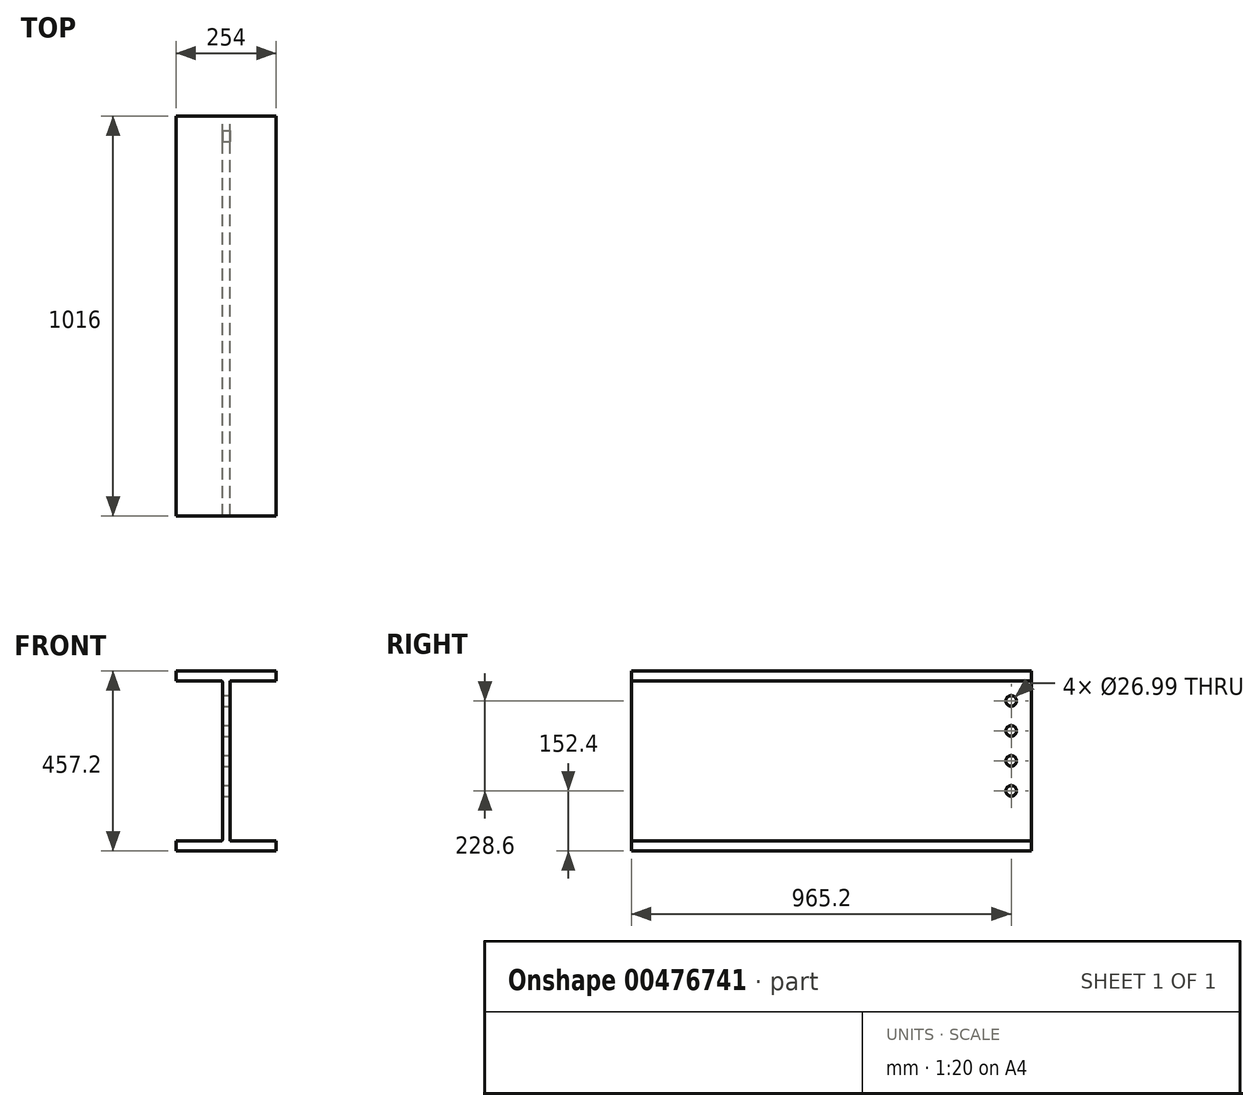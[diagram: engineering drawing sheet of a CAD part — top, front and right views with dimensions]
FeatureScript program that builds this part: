
annotation { "Feature Type Name" : "Feature", "Feature Type Description" : "" }
export const myFeature = defineFeature(function(context is Context, id is Id, definition is map)
    precondition{}
    {
        {
            var Q0;
            Q0=qCreatedBy(makeId("Front.planeOp"),FACE);
            var sketch = newSketch(context, id + "F0", { "sketchPlane" : qUnion([Q0])});
            skLineSegment(sketch, "E0", {"start": v(127, -203.2) * mm, "end": v(12.06, -203.2) * mm});
            skLineSegment(sketch, "E1", {"start": v(9.52, -200.66) * mm, "end": v(9.52, 200.66) * mm});
            skLineSegment(sketch, "E2", {"start": v(12.06, 203.2) * mm, "end": v(127, 203.2) * mm});
            skLineSegment(sketch, "E3", {"start": v(-127, 203.2) * mm, "end": v(-12.06, 203.2) * mm});
            skLineSegment(sketch, "E4", {"start": v(-9.53, 200.66) * mm, "end": v(-9.53, -200.66) * mm});
            skLineSegment(sketch, "E5", {"start": v(-12.06, -203.2) * mm, "end": v(-127, -203.2) * mm});
            skLineSegment(sketch, "E6", {"start": v(0, 0) * mm, "end": v(-9.52, 0) * mm, "construction": true});
            skLineSegment(sketch, "E7", {"start": v(0, 0) * mm, "end": v(9.52, 0) * mm, "construction": true});
            skLineSegment(sketch, "E8", {"start": v(0, 0) * mm, "end": v(0, 228.6) * mm, "construction": true});
            skLineSegment(sketch, "E9", {"start": v(0, 0) * mm, "end": v(0, -228.6) * mm, "construction": true});
            skPoint(sketch, "E10.visualSharp", {"position": v(-9.53, 203.2) * mm});
            skArc(sketch, "E10.filletArc", {"start": v(-9.52, 200.66) * mm, "mid": v(-10.27, 202.46) * mm, "end": v(-12.06, 203.2) * mm});
            skPoint(sketch, "E11.visualSharp", {"position": v(9.53, 203.2) * mm});
            skArc(sketch, "E11.filletArc", {"start": v(12.06, 203.2) * mm, "mid": v(10.27, 202.46) * mm, "end": v(9.52, 200.66) * mm});
            skPoint(sketch, "E12.visualSharp", {"position": v(9.53, -203.2) * mm});
            skArc(sketch, "E12.filletArc", {"start": v(9.52, -200.66) * mm, "mid": v(10.27, -202.46) * mm, "end": v(12.06, -203.2) * mm});
            skPoint(sketch, "E13.visualSharp", {"position": v(-9.53, -203.2) * mm});
            skArc(sketch, "E13.filletArc", {"start": v(-12.06, -203.2) * mm, "mid": v(-10.27, -202.46) * mm, "end": v(-9.52, -200.66) * mm});
            skPoint(sketch, "E14.visualSharp", {"position": v(-127, 228.6) * mm});
            skPoint(sketch, "E15.visualSharp", {"position": v(127, 228.6) * mm});
            skPoint(sketch, "E16.visualSharp", {"position": v(127, 203.2) * mm});
            skPoint(sketch, "E17.visualSharp", {"position": v(127, -228.6) * mm});
            skPoint(sketch, "E18.visualSharp", {"position": v(-127, -203.2) * mm});
            skPoint(sketch, "E19.visualSharp", {"position": v(-127, -228.6) * mm});
            skLineSegment(sketch, "E20", {"start": v(127, -203.2) * mm, "end": v(127, -228.6) * mm});
            skLineSegment(sketch, "E21", {"start": v(-127, -203.2) * mm, "end": v(-127, -228.6) * mm});
            skLineSegment(sketch, "E22", {"start": v(-127, 228.6) * mm, "end": v(-127, 203.2) * mm});
            skLineSegment(sketch, "E23", {"start": v(127, 228.6) * mm, "end": v(127, 203.2) * mm});
            skLineSegment(sketch, "E24", {"start": v(-127, 228.6) * mm, "end": v(127, 228.6) * mm});
            skLineSegment(sketch, "E25", {"start": v(-127, -228.6) * mm, "end": v(127, -228.6) * mm});
            skSolve(sketch);
        }
        {
            var Q0;
            Q0=makeQuery(id+"F0.imprint","IMPRINT",FACE,{"disambiguationData":[TD([[makeQuery(id+"F0.imprint","IMPRINT",EDGE,{"derivedFrom":sQuery(id+"F0.wireOp",EDGE,"E0")}),1.0]])]});
            extrude(context, id + "F1", {"entities" : qUnion([Q0]), "endBound" : BoundingType.SYMMETRIC, "depth" : 1016 * mm});
        }
        {
            var Q0;
            Q0=makeQuery(id+"F1.opExtrude","SWEPT_FACE",FACE,{"disambiguationData":[OSD([sQuery(id+"F0.wireOp",EDGE,"E1")])]});
            var sketch = newSketch(context, id + "F2", { "sketchPlane" : qUnion([Q0])});
            skPoint(sketch, "E26", {"position": v(457.2, 152.4) * mm});
            skPoint(sketch, "E27", {"position": v(457.2, 76.2) * mm});
            skPoint(sketch, "E28", {"position": v(457.2, 0) * mm});
            skPoint(sketch, "E29", {"position": v(457.2, -76.2) * mm});
            skSolve(sketch);
        }
        {
            var Q0;
            Q0=sQuery(id+"F2.wireOp",VERTEX,"E26");
            var Q1;
            Q1=sQuery(id+"F2.wireOp",VERTEX,"E27");
            var Q2;
            Q2=sQuery(id+"F2.wireOp",VERTEX,"E28");
            var Q3;
            Q3=sQuery(id+"F2.wireOp",VERTEX,"E29");
            var Q4;
            Q4=makeQuery(id+"F1.opExtrude","SWEPT_BODY",BODY,{"disambiguationData":[OSD([sQuery(id+"F0.wireOp",EDGE,"E0"),sQuery(id+"F0.wireOp",EDGE,"E1"),sQuery(id+"F0.wireOp",EDGE,"E2"),sQuery(id+"F0.wireOp",EDGE,"E3"),sQuery(id+"F0.wireOp",EDGE,"E4"),sQuery(id+"F0.wireOp",EDGE,"E5"),sQuery(id+"F0.wireOp",EDGE,"E10.filletArc"),sQuery(id+"F0.wireOp",EDGE,"E11.filletArc"),sQuery(id+"F0.wireOp",EDGE,"E12.filletArc"),sQuery(id+"F0.wireOp",EDGE,"E13.filletArc"),sQuery(id+"F0.wireOp",EDGE,"E20"),sQuery(id+"F0.wireOp",EDGE,"E21"),sQuery(id+"F0.wireOp",EDGE,"E22"),sQuery(id+"F0.wireOp",EDGE,"E23"),sQuery(id+"F0.wireOp",EDGE,"E24"),sQuery(id+"F0.wireOp",EDGE,"E25")])]});
            hole(context, id + "F3", {"style" : HoleStyle.SIMPLE, "endStyle" : HoleEndStyle.THROUGH, "holeDiameter" : 26.99 * mm, "isTappedThrough" : true, "tappedDepth" : 12.7 * mm, "tapClearance" : 3, "locations" : qUnion([Q0, Q1, Q2, Q3]), "scope" : qUnion([Q4])});
        }
    });
